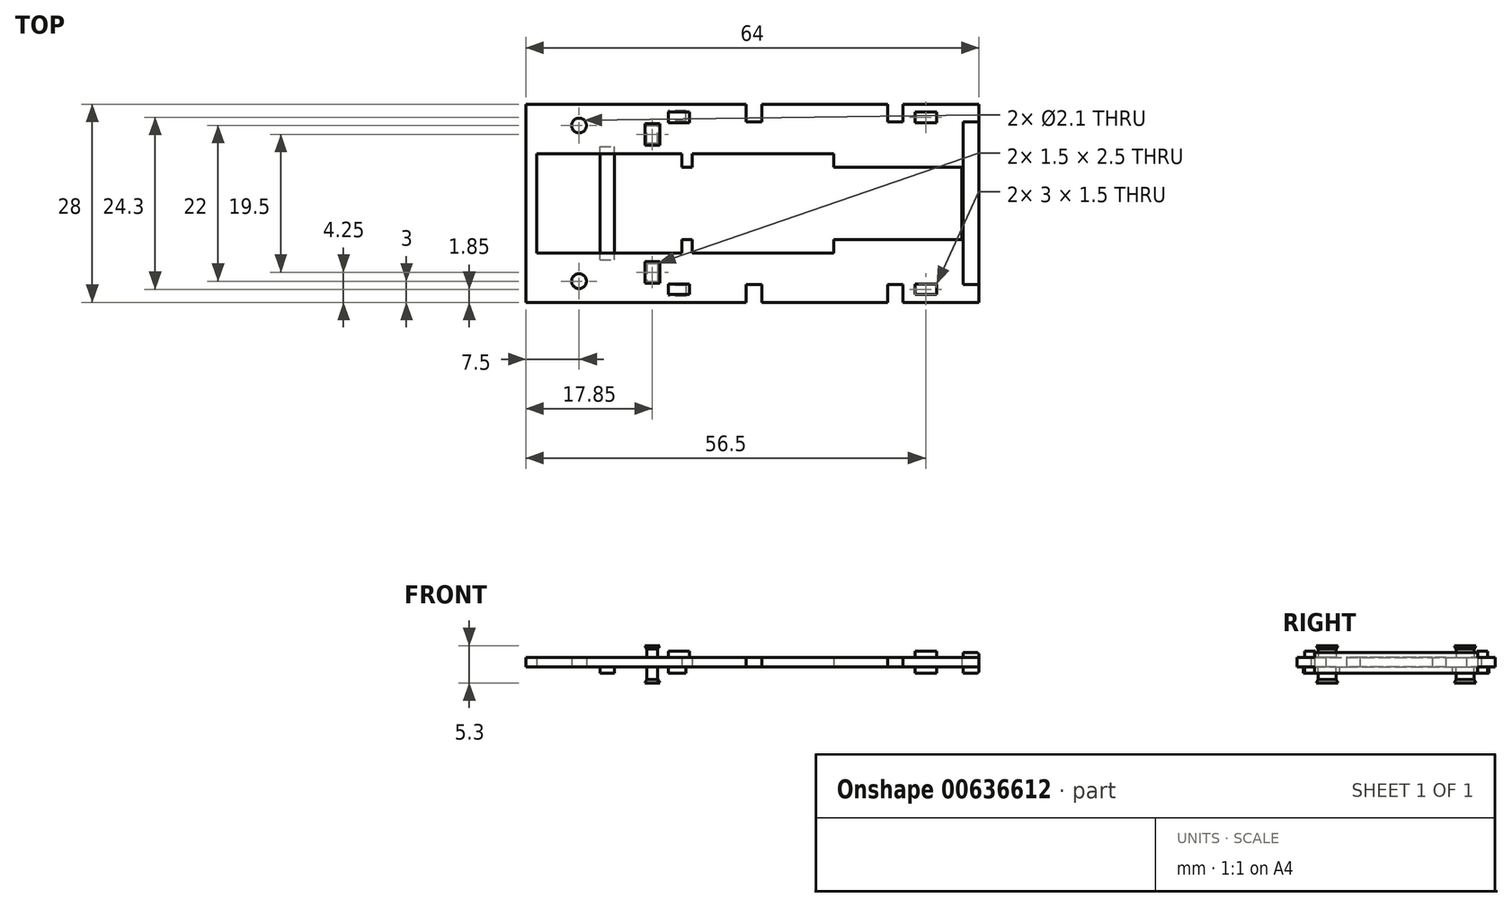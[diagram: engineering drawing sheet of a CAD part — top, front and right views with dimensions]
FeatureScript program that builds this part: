
annotation { "Feature Type Name" : "Feature", "Feature Type Description" : "" }
export const myFeature = defineFeature(function(context is Context, id is Id, definition is map)
    precondition{}
    {
        {
            var Q0;
            Q0=qCreatedBy(makeId("Top.planeOp"),FACE);
            var sketch = newSketch(context, id + "F0", { "sketchPlane" : qUnion([Q0])});
            skLineSegment(sketch, "E0.bottom", {"start": v(32, -14) * mm, "end": v(21.3, -14) * mm});
            skLineSegment(sketch, "E0.top", {"start": v(32, 14) * mm, "end": v(21.3, 14) * mm});
            skLineSegment(sketch, "E0.left", {"start": v(32, -14) * mm, "end": v(32, 14) * mm});
            skLineSegment(sketch, "E0.right", {"start": v(-32, -14) * mm, "end": v(-32, 14) * mm});
            skPoint(sketch, "E0.middle", {"position": v(0, 0) * mm});
            skLineSegment(sketch, "E1.bottom", {"start": v(-10, 5.1) * mm, "end": v(-8.5, 5.1) * mm});
            skLineSegment(sketch, "E1.top", {"start": v(-10, -5.1) * mm, "end": v(-8.5, -5.1) * mm});
            skLineSegment(sketch, "E1.left", {"start": v(-30.5, 5.1) * mm, "end": v(-30.5, -5.1) * mm});
            skLineSegment(sketch, "E1.right", {"start": v(29.6, 5.1) * mm, "end": v(29.6, -5.1) * mm});
            skLineSegment(sketch, "E2.bottom", {"start": v(-30.5, 7) * mm, "end": v(-10, 7) * mm});
            skLineSegment(sketch, "E2.top", {"start": v(-30.5, -7) * mm, "end": v(-10, -7) * mm});
            skLineSegment(sketch, "E2.left", {"start": v(-30.5, 7) * mm, "end": v(-30.5, 5.1) * mm});
            skLineSegment(sketch, "E2.right", {"start": v(11.5, 7) * mm, "end": v(11.5, 5.1) * mm});
            skLineSegment(sketch, "E3.left", {"start": v(-10, 7) * mm, "end": v(-10, 5.1) * mm});
            skLineSegment(sketch, "E3.right", {"start": v(-8.5, 7) * mm, "end": v(-8.5, 5.1) * mm});
            skLineSegment(sketch, "E4.trimOffspring", {"start": v(-10, -5.1) * mm, "end": v(-10, -7) * mm});
            skLineSegment(sketch, "E5.trimOffspring", {"start": v(11.5, 5.1) * mm, "end": v(29.6, 5.1) * mm});
            skLineSegment(sketch, "E6.trimOffspring", {"start": v(11.5, -5.1) * mm, "end": v(29.6, -5.1) * mm});
            skLineSegment(sketch, "E7.trimOffspring", {"start": v(-8.5, -7) * mm, "end": v(11.5, -7) * mm});
            skLineSegment(sketch, "E8.trimOffspring", {"start": v(-8.5, 7) * mm, "end": v(11.5, 7) * mm});
            skLineSegment(sketch, "E9.trimOffspring", {"start": v(-8.5, -5.1) * mm, "end": v(-8.5, -7) * mm});
            skLineSegment(sketch, "E10.trimOffspring", {"start": v(11.5, -5.1) * mm, "end": v(11.5, -7) * mm});
            skLineSegment(sketch, "E11.trimOffspring", {"start": v(-30.5, -5.1) * mm, "end": v(-30.5, -7) * mm});
            skCircle(sketch, "E12", {"center": v(-24.5, -11) * mm, "radius": 1.05 * mm});
            skCircle(sketch, "E13.MirrorC", {"center": v(-24.5, 11) * mm, "radius": 1.05 * mm});
            skLineSegment(sketch, "E14.bottom", {"start": v(-0.9, -11.5) * mm, "end": v(1.3, -11.5) * mm});
            skLineSegment(sketch, "E14.left", {"start": v(-0.9, -11.5) * mm, "end": v(-0.9, -14) * mm});
            skLineSegment(sketch, "E14.right", {"start": v(1.3, -11.5) * mm, "end": v(1.3, -14) * mm});
            skLineSegment(sketch, "E15.top", {"start": v(19.1, -11.5) * mm, "end": v(21.3, -11.5) * mm});
            skLineSegment(sketch, "E15.left", {"start": v(19.1, -14) * mm, "end": v(19.1, -11.5) * mm});
            skLineSegment(sketch, "E15.right", {"start": v(21.3, -14) * mm, "end": v(21.3, -11.5) * mm});
            skLineSegment(sketch, "E16.MirrorCS", {"start": v(21.3, 14) * mm, "end": v(21.3, 11.5) * mm});
            skLineSegment(sketch, "E17.MirrorCS", {"start": v(-0.9, 11.5) * mm, "end": v(-0.9, 14) * mm});
            skLineSegment(sketch, "E18.MirrorCS", {"start": v(19.1, 14) * mm, "end": v(19.1, 11.5) * mm});
            skLineSegment(sketch, "E19.MirrorCS", {"start": v(1.3, 11.5) * mm, "end": v(1.3, 14) * mm});
            skLineSegment(sketch, "E20.MirrorCS", {"start": v(19.1, 11.5) * mm, "end": v(21.3, 11.5) * mm});
            skLineSegment(sketch, "E21.MirrorCS", {"start": v(-0.9, 11.5) * mm, "end": v(1.3, 11.5) * mm});
            skLineSegment(sketch, "E22.trimOffspring", {"start": v(-0.9, 14) * mm, "end": v(-32, 14) * mm});
            skLineSegment(sketch, "E23.trimOffspring", {"start": v(19.1, 14) * mm, "end": v(1.3, 14) * mm});
            skLineSegment(sketch, "E24.trimOffspring", {"start": v(19.1, -14) * mm, "end": v(1.3, -14) * mm});
            skLineSegment(sketch, "E25.trimOffspring", {"start": v(-0.9, -14) * mm, "end": v(-32, -14) * mm});
            skPoint(sketch, "E26.middle", {"position": v(12.9, 2.69) * mm});
            skSolve(sketch);
        }
        {
            var Q0;
            Q0=makeQuery(id+"F0.imprint","IMPRINT",FACE,{"disambiguationData":[TD([[makeQuery(id+"F0.imprint","IMPRINT",EDGE,{"derivedFrom":sQuery(id+"F0.wireOp",EDGE,"E0.bottom")}),-1.0]])]});
            extrude(context, id + "F1", {"entities" : qUnion([Q0]), "depth" : 1.3 * mm});
        }
        {
            var Q0;
            Q0=makeQuery(id+"F1.opExtrude","CAP_FACE",FACE,{"disambiguationData":[OSD([sQuery(id+"F0.wireOp",EDGE,"E0.bottom"),sQuery(id+"F0.wireOp",EDGE,"E0.top"),sQuery(id+"F0.wireOp",EDGE,"E0.left"),sQuery(id+"F0.wireOp",EDGE,"E0.right"),sQuery(id+"F0.wireOp",EDGE,"E1.bottom"),sQuery(id+"F0.wireOp",EDGE,"E1.top"),sQuery(id+"F0.wireOp",EDGE,"E1.left"),sQuery(id+"F0.wireOp",EDGE,"E1.right"),sQuery(id+"F0.wireOp",EDGE,"E2.bottom"),sQuery(id+"F0.wireOp",EDGE,"E2.top"),sQuery(id+"F0.wireOp",EDGE,"E2.left"),sQuery(id+"F0.wireOp",EDGE,"E2.right"),sQuery(id+"F0.wireOp",EDGE,"E3.left"),sQuery(id+"F0.wireOp",EDGE,"E3.right"),sQuery(id+"F0.wireOp",EDGE,"E4.trimOffspring"),sQuery(id+"F0.wireOp",EDGE,"E5.trimOffspring"),sQuery(id+"F0.wireOp",EDGE,"E6.trimOffspring"),sQuery(id+"F0.wireOp",EDGE,"E7.trimOffspring"),sQuery(id+"F0.wireOp",EDGE,"E8.trimOffspring"),sQuery(id+"F0.wireOp",EDGE,"E9.trimOffspring"),sQuery(id+"F0.wireOp",EDGE,"E10.trimOffspring"),sQuery(id+"F0.wireOp",EDGE,"E11.trimOffspring"),sQuery(id+"F0.wireOp",EDGE,"E12"),sQuery(id+"F0.wireOp",EDGE,"E13.MirrorC"),sQuery(id+"F0.wireOp",EDGE,"E14.bottom"),sQuery(id+"F0.wireOp",EDGE,"E14.left"),sQuery(id+"F0.wireOp",EDGE,"E14.right"),sQuery(id+"F0.wireOp",EDGE,"E15.top"),sQuery(id+"F0.wireOp",EDGE,"E15.left"),sQuery(id+"F0.wireOp",EDGE,"E15.right"),sQuery(id+"F0.wireOp",EDGE,"E16.MirrorCS"),sQuery(id+"F0.wireOp",EDGE,"E17.MirrorCS"),sQuery(id+"F0.wireOp",EDGE,"E18.MirrorCS"),sQuery(id+"F0.wireOp",EDGE,"E19.MirrorCS"),sQuery(id+"F0.wireOp",EDGE,"E20.MirrorCS"),sQuery(id+"F0.wireOp",EDGE,"E21.MirrorCS"),sQuery(id+"F0.wireOp",EDGE,"E22.trimOffspring"),sQuery(id+"F0.wireOp",EDGE,"E23.trimOffspring"),sQuery(id+"F0.wireOp",EDGE,"E24.trimOffspring"),sQuery(id+"F0.wireOp",EDGE,"E25.trimOffspring")])],"isStart":false});
            var sketch = newSketch(context, id + "F2", { "sketchPlane" : qUnion([Q0])});
            skLineSegment(sketch, "E27.bottom", {"start": v(-5.8, -1.39) * mm, "end": v(-6.3, -1.39) * mm});
            skLineSegment(sketch, "E27.top", {"start": v(-5.8, 1.39) * mm, "end": v(-6.3, 1.39) * mm});
            skLineSegment(sketch, "E27.left", {"start": v(-5.8, -1.39) * mm, "end": v(-5.8, 1.39) * mm});
            skLineSegment(sketch, "E27.right", {"start": v(-6.3, -1.39) * mm, "end": v(-6.3, 1.39) * mm});
            skPoint(sketch, "E27.middle", {"position": v(-6.05, 0) * mm});
            skLineSegment(sketch, "E28.bottom", {"start": v(29.7, -11.3) * mm, "end": v(-13.3, -11.3) * mm});
            skLineSegment(sketch, "E28.top", {"start": v(29.7, 11.3) * mm, "end": v(-13.3, 11.3) * mm});
            skLineSegment(sketch, "E28.left", {"start": v(29.7, -11.3) * mm, "end": v(29.7, 11.3) * mm});
            skLineSegment(sketch, "E28.right", {"start": v(-13.3, -11.3) * mm, "end": v(-13.3, 11.3) * mm});
            skPoint(sketch, "E28.middle", {"position": v(8.2, 0) * mm});
            skLineSegment(sketch, "E29.bottom", {"start": v(-5.6, -0.5) * mm, "end": v(-6.5, -0.5) * mm});
            skLineSegment(sketch, "E29.top", {"start": v(-5.6, 0.5) * mm, "end": v(-6.5, 0.5) * mm});
            skLineSegment(sketch, "E29.left", {"start": v(-5.6, -0.5) * mm, "end": v(-5.6, 0.5) * mm});
            skLineSegment(sketch, "E29.right", {"start": v(-6.5, -0.5) * mm, "end": v(-6.5, 0.5) * mm});
            skSolve(sketch);
        }
        {
            var Q0;
            {var subQ1=sQuery(id+"F2.wireOp",EDGE,"E28.bottom");Q0=makeQuery(id+"F2.imprint","IMPRINT",FACE,{"disambiguationData":[TD([[makeQuery(id+"F2.imprint","IMPRINT",EDGE,{"derivedFrom":subQ1}),1.0]])]});}
            var sketch = newSketch(context, id + "F3", { "sketchPlane" : qUnion([Q0])});
            skLineSegment(sketch, "E30.bottom", {"start": v(32, -11.5) * mm, "end": v(29.8, -11.5) * mm});
            skLineSegment(sketch, "E30.top", {"start": v(32, 11.5) * mm, "end": v(29.8, 11.5) * mm});
            skLineSegment(sketch, "E30.left", {"start": v(32, -11.5) * mm, "end": v(32, 11.5) * mm});
            skLineSegment(sketch, "E30.right", {"start": v(29.8, -11.5) * mm, "end": v(29.8, 11.5) * mm});
            skPoint(sketch, "E30.middle", {"position": v(30.9, 0) * mm});
            skLineSegment(sketch, "E31.bottom", {"start": v(23, 12.9) * mm, "end": v(26, 12.9) * mm});
            skLineSegment(sketch, "E31.top", {"start": v(23, 11.4) * mm, "end": v(26, 11.4) * mm});
            skLineSegment(sketch, "E31.left", {"start": v(23, 12.9) * mm, "end": v(23, 11.4) * mm});
            skLineSegment(sketch, "E31.right", {"start": v(26, 12.9) * mm, "end": v(26, 11.4) * mm});
            skLineSegment(sketch, "E32.MirrorCS", {"start": v(23, -11.4) * mm, "end": v(26, -11.4) * mm});
            skLineSegment(sketch, "E33.MirrorCS", {"start": v(23, -12.9) * mm, "end": v(23, -11.4) * mm});
            skLineSegment(sketch, "E34.MirrorCS", {"start": v(23, -12.9) * mm, "end": v(26, -12.9) * mm});
            skLineSegment(sketch, "E35.MirrorCS", {"start": v(26, -12.9) * mm, "end": v(26, -11.4) * mm});
            skLineSegment(sketch, "E36.bottom", {"start": v(-14.9, -8.5) * mm, "end": v(-13.4, -8.5) * mm});
            skLineSegment(sketch, "E36.top", {"start": v(-14.9, -11) * mm, "end": v(-13.4, -11) * mm});
            skLineSegment(sketch, "E36.left", {"start": v(-14.9, -8.5) * mm, "end": v(-14.9, -11) * mm});
            skLineSegment(sketch, "E36.right", {"start": v(-13.4, -8.5) * mm, "end": v(-13.4, -11) * mm});
            skLineSegment(sketch, "E37.bottom", {"start": v(-11.9, -11.4) * mm, "end": v(-8.9, -11.4) * mm});
            skLineSegment(sketch, "E37.top", {"start": v(-11.9, -12.9) * mm, "end": v(-8.9, -12.9) * mm});
            skLineSegment(sketch, "E37.left", {"start": v(-11.9, -11.4) * mm, "end": v(-11.9, -12.9) * mm});
            skLineSegment(sketch, "E37.right", {"start": v(-8.9, -11.4) * mm, "end": v(-8.9, -12.9) * mm});
            skLineSegment(sketch, "E38.MirrorCS", {"start": v(-11.9, 11.4) * mm, "end": v(-11.9, 12.9) * mm});
            skLineSegment(sketch, "E39.MirrorCS", {"start": v(-8.9, 11.4) * mm, "end": v(-8.9, 12.9) * mm});
            skLineSegment(sketch, "E40.MirrorCS", {"start": v(-11.9, 11.4) * mm, "end": v(-8.9, 11.4) * mm});
            skLineSegment(sketch, "E41.MirrorCS", {"start": v(-11.9, 12.9) * mm, "end": v(-8.9, 12.9) * mm});
            skLineSegment(sketch, "E42.MirrorCS", {"start": v(-14.9, 11) * mm, "end": v(-13.4, 11) * mm});
            skLineSegment(sketch, "E43.MirrorCS", {"start": v(-14.9, 8.5) * mm, "end": v(-14.9, 11) * mm});
            skLineSegment(sketch, "E44.MirrorCS", {"start": v(-14.9, 8.5) * mm, "end": v(-13.4, 8.5) * mm});
            skLineSegment(sketch, "E45.MirrorCS", {"start": v(-13.4, 8.5) * mm, "end": v(-13.4, 11) * mm});
            skSolve(sketch);
        }
        {
            var Q0;
            Q0=makeQuery(id+"F3.imprint","IMPRINT",FACE,{"disambiguationData":[TD([[makeQuery(id+"F3.imprint","IMPRINT",EDGE,{"derivedFrom":sQuery(id+"F3.wireOp",EDGE,"E30.bottom")}),-1.0]])]});
            extrude(context, id + "F4", {"entities" : qUnion([Q0]), "operationType" : NewBodyOperationType.ADD, "depth" : 0.7 * mm, "offsetDistance" : 25 * mm});
        }
        {
            var Q0;
            Q0=makeQuery(id+"F1.opExtrude","CAP_FACE",FACE,{"disambiguationData":[OSD([sQuery(id+"F0.wireOp",EDGE,"E0.bottom"),sQuery(id+"F0.wireOp",EDGE,"E0.top"),sQuery(id+"F0.wireOp",EDGE,"E0.left"),sQuery(id+"F0.wireOp",EDGE,"E0.right"),sQuery(id+"F0.wireOp",EDGE,"E1.bottom"),sQuery(id+"F0.wireOp",EDGE,"E1.top"),sQuery(id+"F0.wireOp",EDGE,"E1.left"),sQuery(id+"F0.wireOp",EDGE,"E1.right"),sQuery(id+"F0.wireOp",EDGE,"E2.bottom"),sQuery(id+"F0.wireOp",EDGE,"E2.top"),sQuery(id+"F0.wireOp",EDGE,"E2.left"),sQuery(id+"F0.wireOp",EDGE,"E2.right"),sQuery(id+"F0.wireOp",EDGE,"E3.left"),sQuery(id+"F0.wireOp",EDGE,"E3.right"),sQuery(id+"F0.wireOp",EDGE,"E4.trimOffspring"),sQuery(id+"F0.wireOp",EDGE,"E5.trimOffspring"),sQuery(id+"F0.wireOp",EDGE,"E6.trimOffspring"),sQuery(id+"F0.wireOp",EDGE,"E7.trimOffspring"),sQuery(id+"F0.wireOp",EDGE,"E8.trimOffspring"),sQuery(id+"F0.wireOp",EDGE,"E9.trimOffspring"),sQuery(id+"F0.wireOp",EDGE,"E10.trimOffspring"),sQuery(id+"F0.wireOp",EDGE,"E11.trimOffspring"),sQuery(id+"F0.wireOp",EDGE,"E12"),sQuery(id+"F0.wireOp",EDGE,"E13.MirrorC"),sQuery(id+"F0.wireOp",EDGE,"E14.bottom"),sQuery(id+"F0.wireOp",EDGE,"E14.left"),sQuery(id+"F0.wireOp",EDGE,"E14.right"),sQuery(id+"F0.wireOp",EDGE,"E15.top"),sQuery(id+"F0.wireOp",EDGE,"E15.left"),sQuery(id+"F0.wireOp",EDGE,"E15.right"),sQuery(id+"F0.wireOp",EDGE,"E16.MirrorCS"),sQuery(id+"F0.wireOp",EDGE,"E17.MirrorCS"),sQuery(id+"F0.wireOp",EDGE,"E18.MirrorCS"),sQuery(id+"F0.wireOp",EDGE,"E19.MirrorCS"),sQuery(id+"F0.wireOp",EDGE,"E20.MirrorCS"),sQuery(id+"F0.wireOp",EDGE,"E21.MirrorCS"),sQuery(id+"F0.wireOp",EDGE,"E22.trimOffspring"),sQuery(id+"F0.wireOp",EDGE,"E23.trimOffspring"),sQuery(id+"F0.wireOp",EDGE,"E24.trimOffspring"),sQuery(id+"F0.wireOp",EDGE,"E25.trimOffspring")])],"isStart":true});
            var sketch = newSketch(context, id + "F5", { "sketchPlane" : qUnion([Q0])});
            skLineSegment(sketch, "E46.bottom", {"start": v(32, 11.5) * mm, "end": v(29.8, 11.5) * mm});
            skLineSegment(sketch, "E46.top", {"start": v(32, -11.5) * mm, "end": v(29.8, -11.5) * mm});
            skLineSegment(sketch, "E46.left", {"start": v(32, 11.5) * mm, "end": v(32, -11.5) * mm});
            skLineSegment(sketch, "E46.right", {"start": v(29.8, 11.5) * mm, "end": v(29.8, -11.5) * mm});
            skPoint(sketch, "E46.middle", {"position": v(30.9, 0) * mm});
            skPoint(sketch, "E46.middle.positionSnap0", {"position": v(32, 0) * mm});
            skPoint(sketch, "E46.centerSnap0", {"position": v(32, 0) * mm});
            skLineSegment(sketch, "E47.bottom", {"start": v(26, 11.4) * mm, "end": v(23, 11.4) * mm});
            skLineSegment(sketch, "E47.top", {"start": v(26, 12.9) * mm, "end": v(23, 12.9) * mm});
            skLineSegment(sketch, "E47.left", {"start": v(26, 11.4) * mm, "end": v(26, 12.9) * mm});
            skLineSegment(sketch, "E47.right", {"start": v(23, 11.4) * mm, "end": v(23, 12.9) * mm});
            skLineSegment(sketch, "E48.bottom", {"start": v(-13.4, 8.5) * mm, "end": v(-14.9, 8.5) * mm});
            skLineSegment(sketch, "E48.top", {"start": v(-13.4, 11) * mm, "end": v(-14.9, 11) * mm});
            skLineSegment(sketch, "E48.left", {"start": v(-13.4, 8.5) * mm, "end": v(-13.4, 11) * mm});
            skLineSegment(sketch, "E48.right", {"start": v(-14.9, 8.5) * mm, "end": v(-14.9, 11) * mm});
            skLineSegment(sketch, "E49.bottom", {"start": v(-9.4, 11.6) * mm, "end": v(-11.9, 11.6) * mm});
            skLineSegment(sketch, "E49.top", {"start": v(-9.4, 13.1) * mm, "end": v(-11.9, 13.1) * mm});
            skLineSegment(sketch, "E49.left", {"start": v(-9.4, 11.6) * mm, "end": v(-9.4, 13.1) * mm});
            skLineSegment(sketch, "E49.right", {"start": v(-11.9, 11.6) * mm, "end": v(-11.9, 13.1) * mm});
            skLineSegment(sketch, "E50.MirrorCS", {"start": v(-13.4, -11) * mm, "end": v(-14.9, -11) * mm});
            skLineSegment(sketch, "E51.MirrorCS", {"start": v(23, -11.4) * mm, "end": v(23, -12.9) * mm});
            skLineSegment(sketch, "E52.MirrorCS", {"start": v(-11.9, -11.6) * mm, "end": v(-11.9, -13.1) * mm});
            skLineSegment(sketch, "E53.MirrorCS", {"start": v(-9.4, -11.6) * mm, "end": v(-9.4, -13.1) * mm});
            skLineSegment(sketch, "E54.MirrorCS", {"start": v(-13.4, -8.5) * mm, "end": v(-14.9, -8.5) * mm});
            skLineSegment(sketch, "E55.MirrorCS", {"start": v(26, -11.4) * mm, "end": v(26, -12.9) * mm});
            skLineSegment(sketch, "E56.MirrorCS", {"start": v(-13.4, -8.5) * mm, "end": v(-13.4, -11) * mm});
            skLineSegment(sketch, "E57.MirrorCS", {"start": v(-9.4, -13.1) * mm, "end": v(-11.9, -13.1) * mm});
            skLineSegment(sketch, "E58.MirrorCS", {"start": v(26, -11.4) * mm, "end": v(23, -11.4) * mm});
            skLineSegment(sketch, "E59.MirrorCS", {"start": v(-14.9, -8.5) * mm, "end": v(-14.9, -11) * mm});
            skLineSegment(sketch, "E60.MirrorCS", {"start": v(26, -12.9) * mm, "end": v(23, -12.9) * mm});
            skLineSegment(sketch, "E61.MirrorCS", {"start": v(-9.4, -11.6) * mm, "end": v(-11.9, -11.6) * mm});
            skSolve(sketch);
        }
        {
            var Q0;
            Q0=makeQuery(id+"F5.imprint","IMPRINT",FACE,{"disambiguationData":[TD([[makeQuery(id+"F5.imprint","IMPRINT",EDGE,{"derivedFrom":sQuery(id+"F5.wireOp",EDGE,"E49.bottom")}),-1.0]])]});
            var Q1;
            Q1=makeQuery(id+"F5.imprint","IMPRINT",FACE,{"disambiguationData":[TD([[makeQuery(id+"F5.imprint","IMPRINT",EDGE,{"derivedFrom":sQuery(id+"F5.wireOp",EDGE,"E52.MirrorCS")}),1.0]])]});
            var Q2;
            Q2=makeQuery(id+"F5.imprint","IMPRINT",FACE,{"disambiguationData":[TD([[makeQuery(id+"F5.imprint","IMPRINT",EDGE,{"derivedFrom":sQuery(id+"F5.wireOp",EDGE,"E51.MirrorCS")}),1.0]])]});
            var Q3;
            Q3=makeQuery(id+"F5.imprint","IMPRINT",FACE,{"disambiguationData":[TD([[makeQuery(id+"F5.imprint","IMPRINT",EDGE,{"derivedFrom":sQuery(id+"F5.wireOp",EDGE,"E46.bottom")}),1.0]])]});
            var Q4;
            Q4=makeQuery(id+"F5.imprint","IMPRINT",FACE,{"disambiguationData":[TD([[makeQuery(id+"F5.imprint","IMPRINT",EDGE,{"derivedFrom":sQuery(id+"F5.wireOp",EDGE,"E47.bottom")}),-1.0]])]});
            extrude(context, id + "F6", {"entities" : qUnion([Q0, Q1, Q2, Q3, Q4]), "operationType" : NewBodyOperationType.ADD, "depth" : 0.9 * mm, "offsetDistance" : 25 * mm});
        }
        {
            var Q0;
            Q0=makeQuery(id+"F6.opExtrude","CAP_EDGE",EDGE,{"disambiguationData":[OSD([sQuery(id+"F5.wireOp",EDGE,"E46.left")])],"isStart":false});
            fillet(context, id + "F7", {"entities" : qUnion([Q0]), "radius" : 0.3 * mm, "tangentPropagation" : true, "allowEdgeOverflow" : false});
        }
        {
            var Q0;
            Q0=makeQuery(id+"F4.opExtrude","CAP_EDGE",EDGE,{"disambiguationData":[OSD([sQuery(id+"F3.wireOp",EDGE,"E30.left")])],"isStart":false});
            fillet(context, id + "F8", {"entities" : qUnion([Q0]), "radius" : 0.3 * mm, "tangentPropagation" : true, "allowEdgeOverflow" : false});
        }
        {
            var Q0;
            Q0=makeQuery(id+"F1.opExtrude","CAP_FACE",FACE,{"disambiguationData":[OSD([sQuery(id+"F0.wireOp",EDGE,"E0.bottom"),sQuery(id+"F0.wireOp",EDGE,"E0.top"),sQuery(id+"F0.wireOp",EDGE,"E0.left"),sQuery(id+"F0.wireOp",EDGE,"E0.right"),sQuery(id+"F0.wireOp",EDGE,"E1.bottom"),sQuery(id+"F0.wireOp",EDGE,"E1.top"),sQuery(id+"F0.wireOp",EDGE,"E1.left"),sQuery(id+"F0.wireOp",EDGE,"E1.right"),sQuery(id+"F0.wireOp",EDGE,"E2.bottom"),sQuery(id+"F0.wireOp",EDGE,"E2.top"),sQuery(id+"F0.wireOp",EDGE,"E2.left"),sQuery(id+"F0.wireOp",EDGE,"E2.right"),sQuery(id+"F0.wireOp",EDGE,"E3.left"),sQuery(id+"F0.wireOp",EDGE,"E3.right"),sQuery(id+"F0.wireOp",EDGE,"E4.trimOffspring"),sQuery(id+"F0.wireOp",EDGE,"E5.trimOffspring"),sQuery(id+"F0.wireOp",EDGE,"E6.trimOffspring"),sQuery(id+"F0.wireOp",EDGE,"E7.trimOffspring"),sQuery(id+"F0.wireOp",EDGE,"E8.trimOffspring"),sQuery(id+"F0.wireOp",EDGE,"E9.trimOffspring"),sQuery(id+"F0.wireOp",EDGE,"E10.trimOffspring"),sQuery(id+"F0.wireOp",EDGE,"E11.trimOffspring"),sQuery(id+"F0.wireOp",EDGE,"E12"),sQuery(id+"F0.wireOp",EDGE,"E13.MirrorC"),sQuery(id+"F0.wireOp",EDGE,"E14.bottom"),sQuery(id+"F0.wireOp",EDGE,"E14.left"),sQuery(id+"F0.wireOp",EDGE,"E14.right"),sQuery(id+"F0.wireOp",EDGE,"E15.top"),sQuery(id+"F0.wireOp",EDGE,"E15.left"),sQuery(id+"F0.wireOp",EDGE,"E15.right"),sQuery(id+"F0.wireOp",EDGE,"E16.MirrorCS"),sQuery(id+"F0.wireOp",EDGE,"E17.MirrorCS"),sQuery(id+"F0.wireOp",EDGE,"E18.MirrorCS"),sQuery(id+"F0.wireOp",EDGE,"E19.MirrorCS"),sQuery(id+"F0.wireOp",EDGE,"E20.MirrorCS"),sQuery(id+"F0.wireOp",EDGE,"E21.MirrorCS"),sQuery(id+"F0.wireOp",EDGE,"E22.trimOffspring"),sQuery(id+"F0.wireOp",EDGE,"E23.trimOffspring"),sQuery(id+"F0.wireOp",EDGE,"E24.trimOffspring"),sQuery(id+"F0.wireOp",EDGE,"E25.trimOffspring")])],"isStart":true});
            var sketch = newSketch(context, id + "F9", { "sketchPlane" : qUnion([Q0])});
            skLineSegment(sketch, "E62.bottom", {"start": v(-21.5, 8) * mm, "end": v(-19.5, 8) * mm});
            skLineSegment(sketch, "E62.top", {"start": v(-21.5, -8) * mm, "end": v(-19.5, -8) * mm});
            skLineSegment(sketch, "E62.left", {"start": v(-21.5, 8) * mm, "end": v(-21.5, -8) * mm});
            skLineSegment(sketch, "E62.right", {"start": v(-19.5, 8) * mm, "end": v(-19.5, -8) * mm});
            skSolve(sketch);
        }
        {
            var Q0;
            {var subQ0=sQuery(id+"F9.wireOp",EDGE,"E62.bottom");Q0=makeQuery(id+"F9.imprint","IMPRINT",FACE,{"disambiguationData":[TD([[makeQuery(id+"F9.imprint","IMPRINT",EDGE,{"derivedFrom":subQ0}),-1.0]])]});}
            var Q1;
            {var subQ0=sQuery(id+"F9.wireOp",EDGE,"E62.top");Q1=makeQuery(id+"F9.imprint","IMPRINT",FACE,{"disambiguationData":[TD([[makeQuery(id+"F9.imprint","IMPRINT",EDGE,{"derivedFrom":subQ0}),1.0]])]});}
            var Q2;
            {var subQ0=sQuery(id+"F9.wireOp",EDGE,"E62.left");var subQ1=makeQuery(id+"F1.opExtrude","CAP_EDGE",EDGE,{"disambiguationData":[OSD([sQuery(id+"F0.wireOp",EDGE,"E2.top")])],"isStart":true});var subQ2=makeQuery(id+"F9.imprint","INTERSECT",VERTEX,{"derivedFrom":[subQ1,subQ0]});Q2=makeQuery(id+"F9.imprint","IMPRINT",FACE,{"disambiguationData":[TD([[makeQuery(id+"F9.imprint","IMPRINT",EDGE,{"disambiguationData":[TD([[subQ2,-1.0]])],"derivedFrom":subQ0}),1.0]])]});}
            extrude(context, id + "F10", {"entities" : qUnion([Q0, Q1, Q2]), "operationType" : NewBodyOperationType.ADD, "depth" : 0.9 * mm, "offsetDistance" : 25 * mm});
        }
        {
            var Q0;
            Q0=makeQuery(id+"F3.imprint","IMPRINT",FACE,{"disambiguationData":[TD([[makeQuery(id+"F3.imprint","IMPRINT",EDGE,{"derivedFrom":sQuery(id+"F3.wireOp",EDGE,"E38.MirrorCS")}),-1.0]])]});
            var Q1;
            Q1=makeQuery(id+"F3.imprint","IMPRINT",FACE,{"disambiguationData":[TD([[makeQuery(id+"F3.imprint","IMPRINT",EDGE,{"derivedFrom":sQuery(id+"F3.wireOp",EDGE,"E37.bottom")}),-1.0]])]});
            var Q2;
            Q2=makeQuery(id+"F3.imprint","IMPRINT",FACE,{"disambiguationData":[TD([[makeQuery(id+"F3.imprint","IMPRINT",EDGE,{"derivedFrom":sQuery(id+"F3.wireOp",EDGE,"E32.MirrorCS")}),-1.0]])]});
            var Q3;
            Q3=makeQuery(id+"F3.imprint","IMPRINT",FACE,{"disambiguationData":[TD([[makeQuery(id+"F3.imprint","IMPRINT",EDGE,{"derivedFrom":sQuery(id+"F3.wireOp",EDGE,"E31.bottom")}),-1.0]])]});
            extrude(context, id + "F11", {"entities" : qUnion([Q0, Q1, Q2, Q3]), "operationType" : NewBodyOperationType.ADD, "depth" : 0.9 * mm, "offsetDistance" : 25 * mm});
        }
        {
            var Q0;
            Q0=makeQuery(id+"F5.imprint","IMPRINT",FACE,{"disambiguationData":[TD([[makeQuery(id+"F5.imprint","IMPRINT",EDGE,{"derivedFrom":sQuery(id+"F5.wireOp",EDGE,"E48.bottom")}),-1.0]])]});
            var Q1;
            Q1=makeQuery(id+"F5.imprint","IMPRINT",FACE,{"disambiguationData":[TD([[makeQuery(id+"F5.imprint","IMPRINT",EDGE,{"derivedFrom":sQuery(id+"F5.wireOp",EDGE,"E50.MirrorCS")}),-1.0]])]});
            extrude(context, id + "F12", {"entities" : qUnion([Q0, Q1]), "operationType" : NewBodyOperationType.ADD, "depth" : 1.8 * mm, "offsetDistance" : 25 * mm});
        }
        {
            var Q0;
            Q0=makeQuery(id+"F12.opExtrude","CAP_FACE",FACE,{"disambiguationData":[OSD([sQuery(id+"F5.wireOp",EDGE,"E50.MirrorCS"),sQuery(id+"F5.wireOp",EDGE,"E54.MirrorCS"),sQuery(id+"F5.wireOp",EDGE,"E56.MirrorCS"),sQuery(id+"F5.wireOp",EDGE,"E59.MirrorCS")])],"isStart":false});
            var sketch = newSketch(context, id + "F13", { "sketchPlane" : qUnion([Q0])});
            skLineSegment(sketch, "E63.bottom", {"start": v(-14.9, 11) * mm, "end": v(-13.4, 11) * mm});
            skLineSegment(sketch, "E63.top", {"start": v(-14.9, 8.5) * mm, "end": v(-13.4, 8.5) * mm});
            skLineSegment(sketch, "E63.left", {"start": v(-14.9, 11) * mm, "end": v(-14.9, 8.5) * mm});
            skLineSegment(sketch, "E63.right", {"start": v(-13.4, 11) * mm, "end": v(-13.4, 8.5) * mm});
            skLineSegment(sketch, "E64.bottom", {"start": v(-14.9, -8.5) * mm, "end": v(-13.4, -8.5) * mm});
            skLineSegment(sketch, "E64.top", {"start": v(-14.9, -11) * mm, "end": v(-13.4, -11) * mm});
            skLineSegment(sketch, "E64.left", {"start": v(-14.9, -8.5) * mm, "end": v(-14.9, -11) * mm});
            skLineSegment(sketch, "E64.right", {"start": v(-13.4, -8.5) * mm, "end": v(-13.4, -11) * mm});
            skSolve(sketch);
        }
        {
            var Q0;
            Q0 = qSketchRegion(id + "F13", true);
            extrude(context, id + "F14", {"entities" : qUnion([Q0]), "operationType" : NewBodyOperationType.ADD, "depth" : 0.5 * mm, "offsetDistance" : 25 * mm, "hasDraft" : true, "draftAngle" : 30 * degree});
        }
        {
            var Q0;
            Q0=makeQuery(id+"F3.imprint","IMPRINT",FACE,{"disambiguationData":[TD([[makeQuery(id+"F3.imprint","IMPRINT",EDGE,{"derivedFrom":sQuery(id+"F3.wireOp",EDGE,"E42.MirrorCS")}),-1.0]])]});
            var Q1;
            Q1=makeQuery(id+"F3.imprint","IMPRINT",FACE,{"disambiguationData":[TD([[makeQuery(id+"F3.imprint","IMPRINT",EDGE,{"derivedFrom":sQuery(id+"F3.wireOp",EDGE,"E36.bottom")}),-1.0]])]});
            extrude(context, id + "F15", {"entities" : qUnion([Q0, Q1]), "operationType" : NewBodyOperationType.ADD, "depth" : 1.2 * mm, "offsetDistance" : 25 * mm});
        }
        {
            var Q0;
            Q0=makeQuery(id+"F15.opExtrude","CAP_FACE",FACE,{"disambiguationData":[OSD([sQuery(id+"F3.wireOp",EDGE,"E42.MirrorCS"),sQuery(id+"F3.wireOp",EDGE,"E43.MirrorCS"),sQuery(id+"F3.wireOp",EDGE,"E44.MirrorCS"),sQuery(id+"F3.wireOp",EDGE,"E45.MirrorCS")])],"isStart":false});
            var sketch = newSketch(context, id + "F16", { "sketchPlane" : qUnion([Q0])});
            skLineSegment(sketch, "E65.bottom", {"start": v(-14.9, 11) * mm, "end": v(-13.4, 11) * mm});
            skLineSegment(sketch, "E65.top", {"start": v(-14.9, 8.5) * mm, "end": v(-13.4, 8.5) * mm});
            skLineSegment(sketch, "E65.left", {"start": v(-14.9, 11) * mm, "end": v(-14.9, 8.5) * mm});
            skLineSegment(sketch, "E65.right", {"start": v(-13.4, 11) * mm, "end": v(-13.4, 8.5) * mm});
            skLineSegment(sketch, "E66.MirrorCS", {"start": v(-14.9, -11) * mm, "end": v(-13.4, -11) * mm});
            skLineSegment(sketch, "E67.MirrorCS", {"start": v(-14.9, -11) * mm, "end": v(-14.9, -8.5) * mm});
            skLineSegment(sketch, "E68.MirrorCS", {"start": v(-13.4, -11) * mm, "end": v(-13.4, -8.5) * mm});
            skLineSegment(sketch, "E69.MirrorCS", {"start": v(-14.9, -8.5) * mm, "end": v(-13.4, -8.5) * mm});
            skSolve(sketch);
        }
        {
            var Q0;
            Q0 = qSketchRegion(id + "F16", true);
            extrude(context, id + "F17", {"entities" : qUnion([Q0]), "operationType" : NewBodyOperationType.ADD, "depth" : 0.5 * mm, "offsetDistance" : 25 * mm, "hasDraft" : true, "draftAngle" : 30 * degree});
        }
    });
